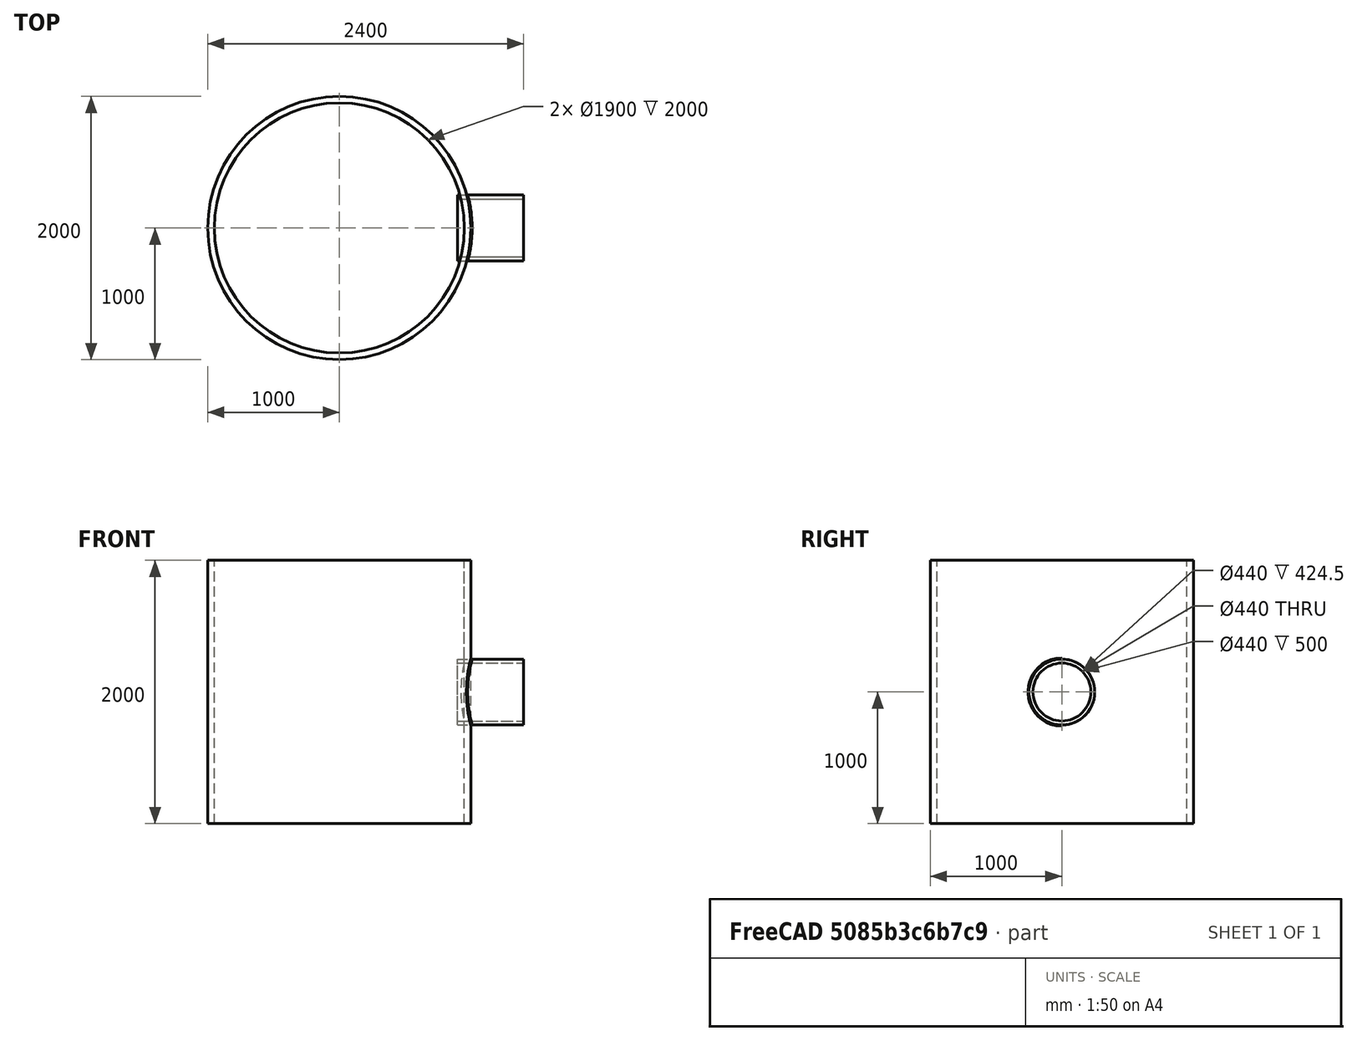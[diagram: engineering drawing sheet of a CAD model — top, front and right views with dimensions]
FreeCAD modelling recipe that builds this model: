
FCSTD DOCUMENT  (FreeCAD 0.21R33694 (Git))
Label: Tubes_Example
License: All rights reserved
LicenseURL: http://en.wikipedia.org/wiki/All_rights_reserved
objects: Part::Feature×3, Part::FeaturePython×2, Fem::FemSolverObjectPython×1, Part::MultiFuse×1, Fem::ConstraintFixed×1, Fem::ConstraintPressure×1, App::MaterialObjectPython×1, Fem::FemMeshObjectPython×1, Fem::FemAnalysis×1, Part::Fillet×1
note: 7 computed .brp shape members not serialized (recipe doc carries the construction recipe); baked Part::Feature solids carry a one-line shape summary decoded from their .brp

FEATURE [Part::FeaturePython] Tube  # WARN: FeaturePython — macro-defined, semantics opaque (R4)
  AttacherType = Attacher::AttachEngine3D
  Height = 2000
  InnerRadius = 950
  OuterRadius = 1000
FEATURE [Fem::FemSolverObjectPython] SolverCcxTools  # FEM object (typed FeaturePython)
  AnalysisType = 0
  BeamShellResultOutput3D = false
  BucklingFactors = 1
  EigenmodeHighLimit = 1000000
  EigenmodeLowLimit = 0
  EigenmodesCount = 10
  GeometricalNonlinearity = 0
  IterationsControlParameterCutb = 0.25,0.5,0.75,0.85,,,1.5,
  IterationsControlParameterIter = 4,8,9,200,10,400,,200,,
  IterationsControlParameterTimeUse = false
  IterationsThermoMechMaximum = 2000
  IterationsUserDefinedIncrementations = false
  IterationsUserDefinedTimeStepLength = false
  MaterialNonlinearity = 0
  MatrixSolverType = 0
  SplitInputWriter = false
  ThermoMechSteadyState = true
  TimeEnd = 1
  TimeInitialStep = 0.01
FEATURE [Part::FeaturePython] Tube001  # WARN: FeaturePython — macro-defined, semantics opaque (R4)
  AttacherType = Attacher::AttachEngine3D
  Height = 500
  InnerRadius = 220
  OuterRadius = 250
  Placement = pos=(900,0,1000) rot=(0,1,0;1.5708rad)
FEATURE [Part::Feature] Solid
  shape: bbox 2000 x 2000 x 2000 mm, 5 faces (baked)
FEATURE [Part::Feature] Solid001
  shape: bbox 83.48 x 500 x 500 mm, 6 faces (baked)
FEATURE [Part::Feature] Solid003
  shape: bbox 431.8 x 500 x 500 mm, 5 faces (baked)
FEATURE [Part::MultiFuse] Fusion
  Shapes = -> [Solid,Solid001,Solid003]
FEATURE [Fem::ConstraintFixed] ConstraintFixed
  NormalDirection = (0,0,1)
  References = -> [Fusion]
  Scale = 44
FEATURE [Fem::ConstraintPressure] ConstraintPressure
  NormalDirection = (1,0,0)
  Pressure = 100
  References = -> [Fusion]
  Reversed = true
  Scale = 24
FEATURE [App::MaterialObjectPython] MaterialSolid  # material (typed FeaturePython)
  Category = 0
  Material = AuthorAndLicense=(c) 2013 Juergen Riegel (CC-BY 3.0),CardName=Steel-Generic,Density=7900 kg/m^3,+9 more (map truncated)
  References = -> [Fusion]
FEATURE [Fem::FemMeshObjectPython] FEMMeshGmsh  # FEM object (typed FeaturePython)
  Algorithm2D = 0
  Algorithm3D = 0
  CharacteristicLengthMax = 100
  CharacteristicLengthMin = 0
  CoherenceMesh = true
  ElementDimension = 0
  ElementOrder = 1
  GeometryTolerance = 1e-06
  GroupsOfNodes = false
  HighOrderOptimize = 0
  MeshSizeFromCurvature = 12
  OptimizeNetgen = false
  OptimizeStd = true
  Part = -> Fusion
  RecombinationAlgorithm = 0
  Recombine3DAll = false
  RecombineAll = false
  SecondOrderLinear = false
FEATURE [Fem::FemAnalysis] Analysis
  Group = -> [SolverCcxTools,ConstraintFixed,ConstraintPressure,MaterialSolid,FEMMeshGmsh]
FEATURE [Part::Fillet] Fillet
  Base = -> Fusion
  Edges = 2 edges r=10: [Edge1,Edge4]
